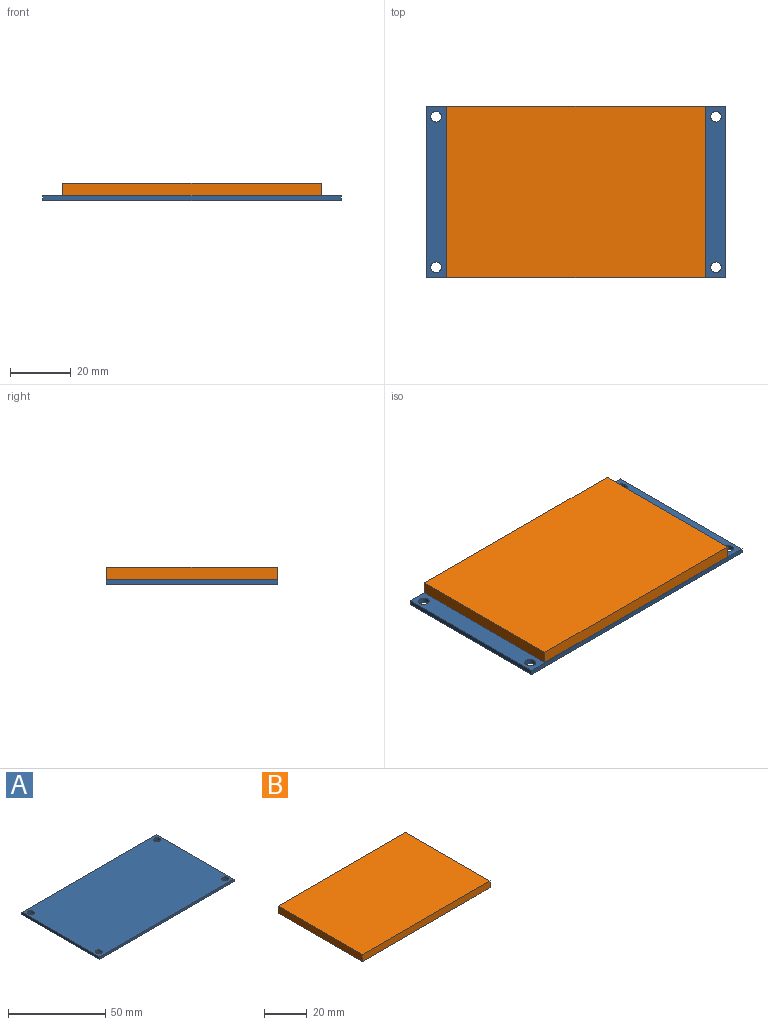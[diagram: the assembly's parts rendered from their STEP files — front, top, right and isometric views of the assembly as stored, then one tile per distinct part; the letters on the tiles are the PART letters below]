
ASSEMBLY  parts=2 mates=1
PART A: 10 faces, bbox 98x56.3x1.6 mm
  f0: plane 56.34x1.6mm, normal (-1,0,0), area 90.1mm2, adj f1,f3,f4,f5
  f1: plane 98x1.6mm, normal (0,-1,0), area 156.8mm2, adj f0,f2,f4,f5
  f2: plane 56.34x1.6mm, normal (1,0,0), area 90.1mm2, adj f1,f3,f4,f5
  f3: plane 98x1.6mm, normal (0,1,0), area 156.8mm2, adj f0,f2,f4,f5
  f4: plane 98x56.34mm, normal (0,0,1), area 5482.8mm2, adj f0,f1,f2,f3,f6,f7,f8,f9
  f5: plane 98x56.34mm, normal (0,0,-1), area 5482.8mm2, adj f0,f1,f2,f3,f6,f7,f8,f9
  f6: cylinder r=1.75mm len=3.5mm, axis (0,0,1), area 17.6mm2, adj f4,f5
  f7: cylinder r=1.75mm len=3.5mm, axis (0,0,1), area 17.6mm2, adj f4,f5
  f8: cylinder r=1.75mm len=3.5mm, axis (0,0,1), area 17.6mm2, adj f4,f5
  f9: cylinder r=1.75mm len=3.5mm, axis (0,0,1), area 17.6mm2, adj f4,f5
PART B: 6 faces, bbox 85x56x4 mm
  f0: plane 56x4mm, normal (-1,0,0), area 224mm2, adj f1,f3,f4,f5
  f1: plane 84.96x4mm, normal (0,-1,0), area 339.8mm2, adj f0,f2,f4,f5
  f2: plane 56x4mm, normal (1,0,0), area 224mm2, adj f1,f3,f4,f5
  f3: plane 84.96x4mm, normal (0,1,0), area 339.8mm2, adj f0,f2,f4,f5
  f4: plane 84.96x56mm, normal (0,0,1), area 4757.8mm2, adj f0,f1,f2,f3
  f5: plane 84.96x56mm, normal (0,0,-1), area 4757.8mm2, adj f0,f1,f2,f3
PLACE A at identity
PLACE B t=(6.52,0.17,1.6)mm
MATE fastened A.f4 <-> B.f5  axis (0,0,1) through (49,28.17,1.6)mm
